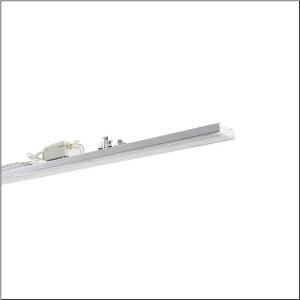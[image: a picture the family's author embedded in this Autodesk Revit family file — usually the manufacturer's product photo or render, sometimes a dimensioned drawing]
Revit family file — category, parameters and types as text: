
# Revit family: licross_r__21_recessed_ho_52te11mn4fxs_d685
name_source: partatom
category: Lighting Fixtures
units: mm (PartAtom-declared; Revit-internal decimal feet)

## family parameters
Cut with Voids When Loaded = No
Host = Face
Light Source = No
Part Type = Normal
Room Calculation Point = No
Round Connector Dimension = Use Diameter
Shared = No

## types (1)
- --- (1 x LED, 15070 lm, 83.1 W, 4000K)
    Apparent Load = 83 VA
    CIE Flux Codes = 87 95 99 100 100
    Color Rendering = 80
    Color Temperature = 4000K
    Default Elevation = 1800 mm
    Description = Licross® 21 Recessed HO, luminaire insert, of sheet steel, galvanised, coil coated, white, length: 1.500mm, width: 66mm, height: 67mm, LED rated luminous flux: 15.060lm, light colour: 840, control gear: ON/OFF Multilumen, with plug, 3-pole, with phase selection, mains connection: 220..240V, AC, 50/60Hz, rated input power: 83W, halogen-free wiring, primary light control with lens, of plastic, primary optical cover: cover, of PMMA, light emission: direct distribution, primary light characteristic: symmetric, protection rating (complete): IP54, insulation class (complete): insulation class I (protective earthing), certification: CE, ENEC, VDE, UKCA, protection symbol: D if used in an environment with non-conductive dust loads with corresponding accessories, impact resistance: IK06, permissible ambient temperature for indoor applications: -35..+30°C, corresponds to IFS (International Featured Standards) requirements for safety and quality in the food industry, reducing of maximum allowable ambient temperature of 5°C with ceiling mounting, LABS conformity tested according to VDMA 24364:2018-05, packaging unit: 1 piece
    Height = 58 mm
    Lamp = 1 x LED
    Lamp Light Flux = 15070 lm
    Lamp Power = 83.1 W
    Lamp count = 1
    Length = 1500 mm
    Luminous efficacy = 181 lm/W
    Manufacturer = Siteco
    ModVariant = No
    Model = 52TE11MN4FXS
    Mounting Place = Ceiling
    Mounting Type = Pendant
    Number of Poles = 1
    OnlyDefault = Yes
    Power Factor = 1
    Product Name = Licross® 21 Recessed HO
    Product group = luminaire insert
    ProductGroupID = 901
    Protection Class = Protection class I
    Protection Degree = IP 54
    RLX_Detail_Level = 1
    RLX_Emergency_Light_Flux = 0 lm
    RLX_Emergency_Type = 0
    RLX_Emergency_Type_DB = No
    RlxData = <blob elided: 22241 chars, md5=02362c9b>
    Socket = socket
    Standby Power = 0 W
    System Light Flux = 15070 lm
    System Power = 83 W
    Type Comments = factory setting: luminous flux: 100 % | (A | C | E) | 195 mA
    Type Image = l_1296930.jpg
    URL = http://relux.com
    VarID = @adj_038177
    Voltage = 0 V
    Weight = 0.00 kg
    Width = 66 mm

## geometry (parser evidence)
native form markers: Blend x4, Sweep x12
no freeform markers — native parametric forms only
